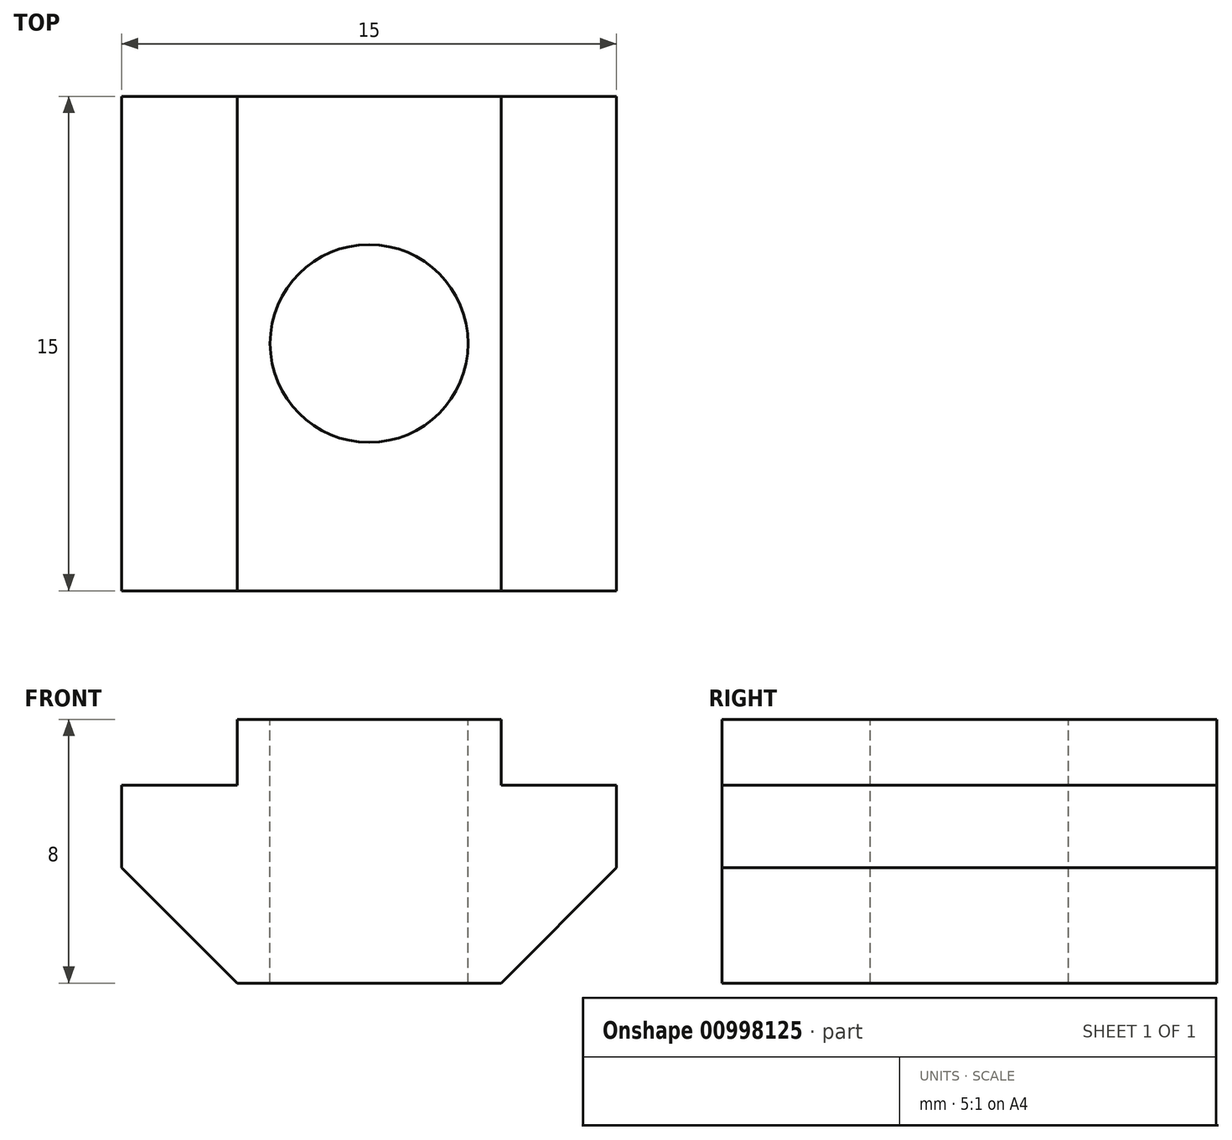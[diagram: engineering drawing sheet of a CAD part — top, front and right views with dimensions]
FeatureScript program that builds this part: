
annotation { "Feature Type Name" : "Feature", "Feature Type Description" : "" }
export const myFeature = defineFeature(function(context is Context, id is Id, definition is map)
    precondition{}
    {
        {
            var Q0;
            Q0=qCreatedBy(makeId("Front.planeOp"),FACE);
            var sketch = newSketch(context, id + "F0", { "sketchPlane" : qUnion([Q0])});
            skLineSegment(sketch, "E0", {"start": v(0, 0) * mm, "end": v(4, 0) * mm});
            skLineSegment(sketch, "E1", {"start": v(4, 0) * mm, "end": v(7.5, 3.5) * mm});
            skLineSegment(sketch, "E2", {"start": v(7.5, 3.5) * mm, "end": v(7.5, 6) * mm});
            skLineSegment(sketch, "E3", {"start": v(7.5, 6) * mm, "end": v(4, 6) * mm});
            skLineSegment(sketch, "E4", {"start": v(4, 6) * mm, "end": v(4, 8) * mm});
            skLineSegment(sketch, "E5", {"start": v(4, 8) * mm, "end": v(0, 8) * mm});
            skLineSegment(sketch, "E6", {"start": v(0, 8) * mm, "end": v(0, 0) * mm, "construction": true});
            skLineSegment(sketch, "E7.MirrorCS", {"start": v(-4, 0) * mm, "end": v(-7.5, 3.5) * mm});
            skLineSegment(sketch, "E8.MirrorCS", {"start": v(-7.5, 3.5) * mm, "end": v(-7.5, 6) * mm});
            skLineSegment(sketch, "E9.MirrorCS", {"start": v(-7.5, 6) * mm, "end": v(-4, 6) * mm});
            skLineSegment(sketch, "E10.MirrorCS", {"start": v(-4, 8) * mm, "end": v(0, 8) * mm});
            skLineSegment(sketch, "E11.MirrorCS", {"start": v(-4, 6) * mm, "end": v(-4, 8) * mm});
            skLineSegment(sketch, "E12.MirrorCS", {"start": v(0, 0) * mm, "end": v(-4, 0) * mm});
            skSolve(sketch);
        }
        {
            var Q0;
            Q0 = qSketchRegion(id + "F0", true);
            extrude(context, id + "F1", {"entities" : qUnion([Q0]), "depth" : 15 * mm, "offsetDistance" : 25 * mm});
        }
        {
            var Q0;
            Q0=makeQuery(id+"F1.opExtrude","SWEPT_FACE",FACE,{"disambiguationData":[OSD([sQuery(id+"F0.wireOp",EDGE,"E5"),sQuery(id+"F0.wireOp",EDGE,"E10.MirrorCS")])]});
            var sketch = newSketch(context, id + "F2", { "sketchPlane" : qUnion([Q0])});
            skLineSegment(sketch, "E13", {"start": v(0, -15) * mm, "end": v(0, 0) * mm, "construction": true});
            skLineSegment(sketch, "E14", {"start": v(-4, -7.5) * mm, "end": v(4, -7.5) * mm, "construction": true});
            skCircle(sketch, "E15", {"center": v(0, -7.5) * mm, "radius": 3 * mm});
            skSolve(sketch);
        }
        {
            var Q0;
            Q0 = qSketchRegion(id + "F2", true);
            extrude(context, id + "F3", {"entities" : qUnion([Q0]), "operationType" : NewBodyOperationType.REMOVE, "endBound" : BoundingType.THROUGH_ALL, "oppositeDirection" : true, "depth" : 25 * mm, "offsetDistance" : 25 * mm});
        }
    });
